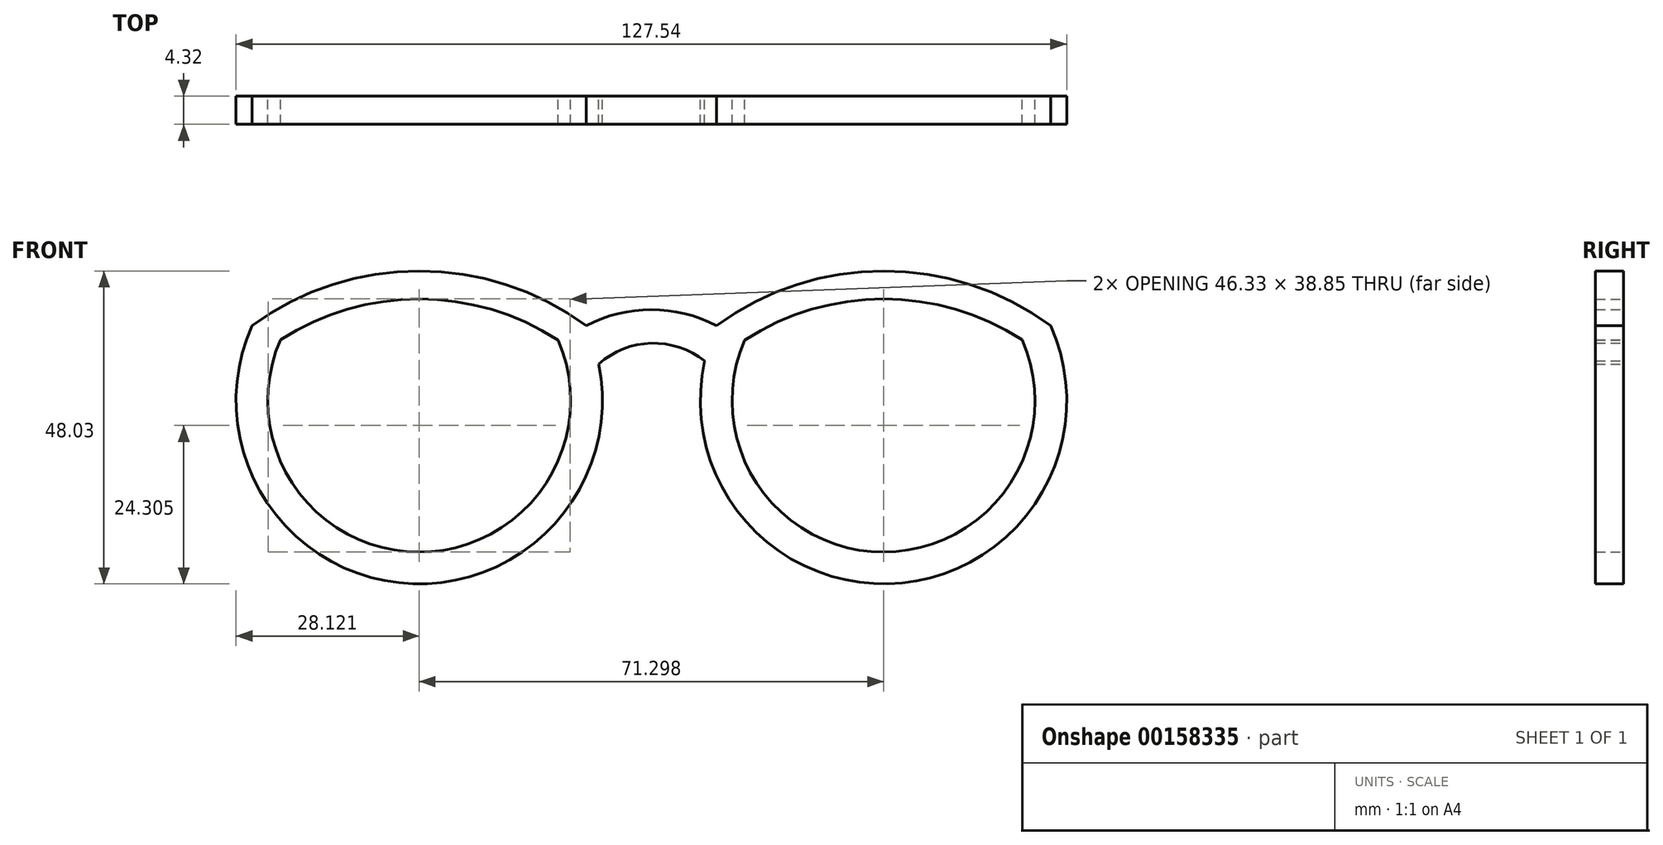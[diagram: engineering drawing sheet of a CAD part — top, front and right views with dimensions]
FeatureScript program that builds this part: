
annotation { "Feature Type Name" : "Feature", "Feature Type Description" : "" }
export const myFeature = defineFeature(function(context is Context, id is Id, definition is map)
    precondition{}
    {
        {
            var Q0;
            Q0=qCreatedBy(makeId("Front.planeOp"),FACE);
            var sketch = newSketch(context, id + "F0", { "sketchPlane" : qUnion([Q0])});
            skArc(sketch, "E0", {"start": v(9.99, 0) * mm, "mid": v(35.65, -39.64) * mm, "end": v(61.3, 0) * mm});
            skArc(sketch, "E1", {"start": v(61.3, 0) * mm, "mid": v(35.65, 8.4) * mm, "end": v(9.99, 0) * mm});
            skArc(sketch, "E2", {"start": v(14.34, -2.22) * mm, "mid": v(35.67, -34.76) * mm, "end": v(56.94, -2.18) * mm});
            skArc(sketch, "E3", {"start": v(56.94, -2.18) * mm, "mid": v(35.63, 4.1) * mm, "end": v(14.34, -2.22) * mm});
            skArc(sketch, "E4.MirrorCS", {"start": v(-61.3, 0) * mm, "mid": v(-35.65, 8.4) * mm, "end": v(-9.99, 0) * mm});
            skArc(sketch, "E5.MirrorCS", {"start": v(-56.94, -2.18) * mm, "mid": v(-35.63, 4.1) * mm, "end": v(-14.34, -2.22) * mm});
            skArc(sketch, "E6.MirrorCS", {"start": v(-9.99, 0) * mm, "mid": v(-35.65, -39.64) * mm, "end": v(-61.3, 0) * mm});
            skArc(sketch, "E7.MirrorCS", {"start": v(-14.34, -2.22) * mm, "mid": v(-35.67, -34.76) * mm, "end": v(-56.94, -2.18) * mm});
            skArc(sketch, "E8", {"start": v(9.99, 0) * mm, "mid": v(0, 2.45) * mm, "end": v(-9.99, 0) * mm});
            skArc(sketch, "E9", {"start": v(8.2, -5.42) * mm, "mid": v(-0.04, -2.7) * mm, "end": v(-8.1, -5.9) * mm});
            skSolve(sketch);
        }
        {
            var Q0;
            Q0 = qSketchRegion(id + "F0", true);
            extrude(context, id + "F1", {"entities" : qUnion([Q0]), "depth" : 4.32 * mm});
        }
    });
